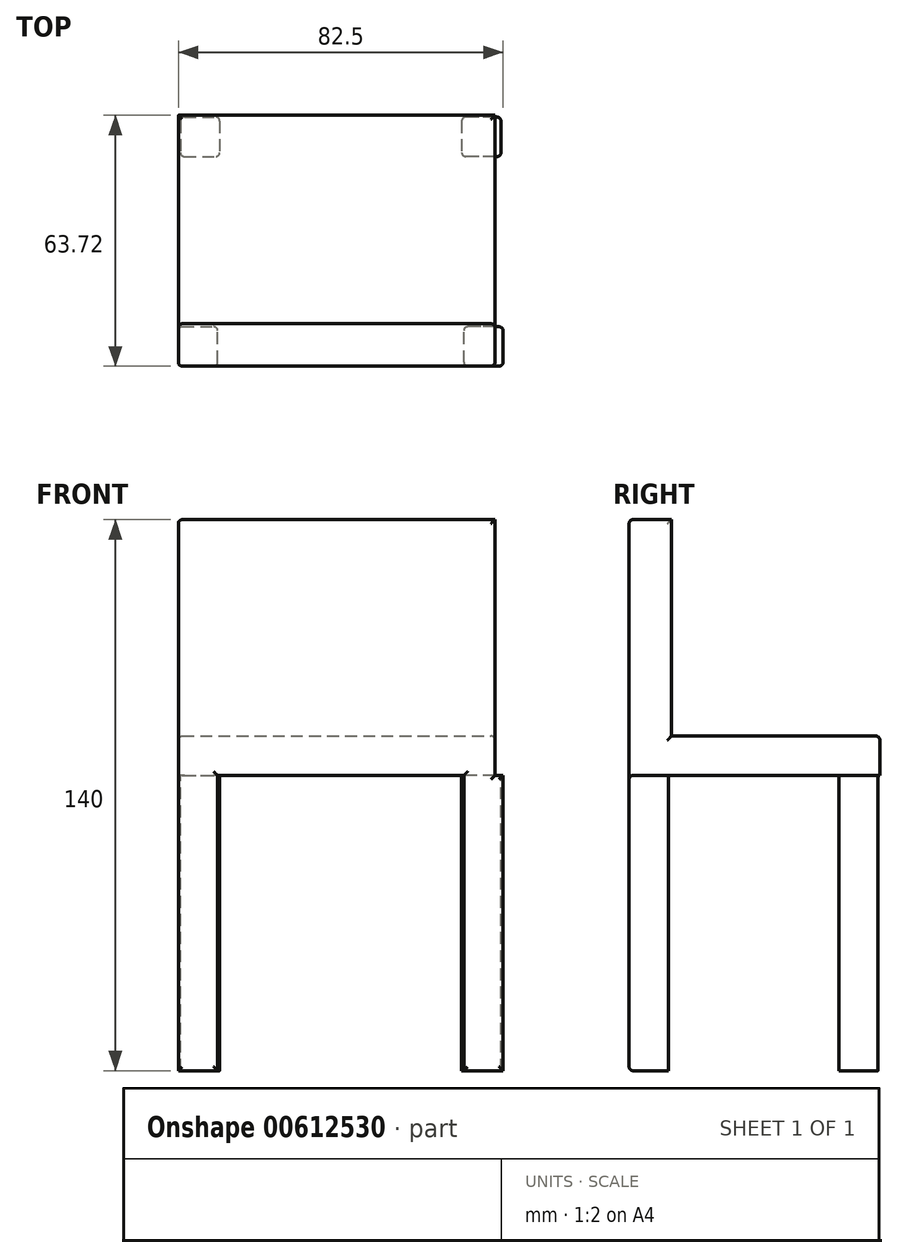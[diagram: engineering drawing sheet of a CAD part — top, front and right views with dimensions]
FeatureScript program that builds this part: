
annotation { "Feature Type Name" : "Feature", "Feature Type Description" : "" }
export const myFeature = defineFeature(function(context is Context, id is Id, definition is map)
    precondition{}
    {
        {
            var Q0;
            Q0=qCreatedBy(makeId("Top.planeOp"),FACE);
            var sketch = newSketch(context, id + "F0", { "sketchPlane" : qUnion([Q0])});
            skLineSegment(sketch, "E0.bottom", {"start": v(39.19, -35.62) * mm, "end": v(-41.25, -35.62) * mm});
            skLineSegment(sketch, "E0.top", {"start": v(39.19, 28.1) * mm, "end": v(-41.25, 28.1) * mm});
            skLineSegment(sketch, "E0.left", {"start": v(39.19, -35.62) * mm, "end": v(39.19, 28.1) * mm});
            skLineSegment(sketch, "E0.right", {"start": v(-41.25, -35.62) * mm, "end": v(-41.25, 28.1) * mm});
            skSolve(sketch);
        }
        {
            var Q0;
            Q0=makeQuery(id+"F0.imprint","IMPRINT",FACE,{"disambiguationData":[TD([[makeQuery(id+"F0.imprint","IMPRINT",EDGE,{"derivedFrom":sQuery(id+"F0.wireOp",EDGE,"E0.bottom")}),-1.0]])]});
            extrude(context, id + "F1", {"entities" : qUnion([Q0]), "depth" : 10 * mm, "offsetDistance" : 25 * mm});
        }
        {
            var Q0;
            Q0=qCreatedBy(makeId("Top.planeOp"),FACE);
            var sketch = newSketch(context, id + "F2", { "sketchPlane" : qUnion([Q0])});
            skLineSegment(sketch, "E1.bottom", {"start": v(-40.74, 27.64) * mm, "end": v(-30.74, 27.64) * mm});
            skLineSegment(sketch, "E1.top", {"start": v(-40.74, 17.64) * mm, "end": v(-30.74, 17.64) * mm});
            skLineSegment(sketch, "E1.left", {"start": v(-40.74, 27.64) * mm, "end": v(-40.74, 17.64) * mm});
            skLineSegment(sketch, "E1.right", {"start": v(-30.74, 27.64) * mm, "end": v(-30.74, 17.64) * mm});
            skSolve(sketch);
        }
        {
            var Q0;
            Q0=makeQuery(id+"F2.imprint","IMPRINT",FACE,{"disambiguationData":[TD([[makeQuery(id+"F2.imprint","IMPRINT",EDGE,{"derivedFrom":sQuery(id+"F2.wireOp",EDGE,"E1.bottom")}),-1.0]])]});
            extrude(context, id + "F3", {"entities" : qUnion([Q0]), "oppositeDirection" : true, "depth" : 75 * mm, "offsetDistance" : 25 * mm});
        }
        {
            var Q0;
            Q0=makeQuery(id+"F1.opExtrude","CAP_FACE",FACE,{"disambiguationData":[OSD([sQuery(id+"F0.wireOp",EDGE,"E0.bottom"),sQuery(id+"F0.wireOp",EDGE,"E0.top"),sQuery(id+"F0.wireOp",EDGE,"E0.left"),sQuery(id+"F0.wireOp",EDGE,"E0.right")])],"isStart":true});
            var sketch = newSketch(context, id + "F4", { "sketchPlane" : qUnion([Q0])});
            skLineSegment(sketch, "E2.bottom", {"start": v(-41.25, 35.62) * mm, "end": v(-31.25, 35.62) * mm});
            skLineSegment(sketch, "E2.top", {"start": v(-41.25, 25.62) * mm, "end": v(-31.25, 25.62) * mm});
            skLineSegment(sketch, "E2.left", {"start": v(-41.25, 35.62) * mm, "end": v(-41.25, 25.62) * mm});
            skLineSegment(sketch, "E2.right", {"start": v(-31.25, 35.62) * mm, "end": v(-31.25, 25.62) * mm});
            skSolve(sketch);
        }
        {
            var Q0;
            Q0=makeQuery(id+"F4.imprint","IMPRINT",FACE,{"disambiguationData":[TD([[makeQuery(id+"F4.imprint","IMPRINT",EDGE,{"derivedFrom":sQuery(id+"F4.wireOp",EDGE,"E2.bottom")}),1.0]])]});
            extrude(context, id + "F5", {"entities" : qUnion([Q0]), "depth" : 75 * mm, "offsetDistance" : 25 * mm});
        }
        {
            var Q0;
            Q0=makeQuery(id+"F3.opExtrude","SWEPT_BODY",BODY,{"disambiguationData":[OSD([sQuery(id+"F2.wireOp",EDGE,"E1.bottom"),sQuery(id+"F2.wireOp",EDGE,"E1.top"),sQuery(id+"F2.wireOp",EDGE,"E1.left"),sQuery(id+"F2.wireOp",EDGE,"E1.right")])]});
            var Q1;
            Q1=makeQuery(id+"F5.opExtrude","SWEPT_BODY",BODY,{"disambiguationData":[OSD([sQuery(id+"F4.wireOp",EDGE,"E2.bottom"),sQuery(id+"F4.wireOp",EDGE,"E2.top"),sQuery(id+"F4.wireOp",EDGE,"E2.left"),sQuery(id+"F4.wireOp",EDGE,"E2.right")])]});
            var Q2;
            Q2=qCreatedBy(makeId("Right.planeOp"),FACE);
            mirror(context, id + "F6", {"operationType" : NewBodyOperationType.ADD, "entities" : qUnion([Q0, Q1]), "mirrorPlane" : qUnion([Q2])});
        }
        {
            var Q0;
            Q0=makeQuery(id+"F1.opExtrude","CAP_FACE",FACE,{"disambiguationData":[OSD([sQuery(id+"F0.wireOp",EDGE,"E0.bottom"),sQuery(id+"F0.wireOp",EDGE,"E0.top"),sQuery(id+"F0.wireOp",EDGE,"E0.left"),sQuery(id+"F0.wireOp",EDGE,"E0.right")])],"isStart":false});
            var sketch = newSketch(context, id + "F7", { "sketchPlane" : qUnion([Q0])});
            skLineSegment(sketch, "E3.bottom", {"start": v(-41.25, -24.86) * mm, "end": v(39.19, -24.86) * mm});
            skLineSegment(sketch, "E3.top", {"start": v(-41.25, -35.62) * mm, "end": v(39.19, -35.62) * mm});
            skLineSegment(sketch, "E3.left", {"start": v(-41.25, -24.86) * mm, "end": v(-41.25, -35.62) * mm});
            skLineSegment(sketch, "E3.right", {"start": v(39.19, -24.86) * mm, "end": v(39.19, -35.62) * mm});
            skSolve(sketch);
        }
        {
            var Q0;
            Q0=makeQuery(id+"F7.imprint","IMPRINT",FACE,{"disambiguationData":[TD([[makeQuery(id+"F7.imprint","IMPRINT",EDGE,{"derivedFrom":sQuery(id+"F7.wireOp",EDGE,"E3.bottom")}),-1.0]])]});
            extrude(context, id + "F8", {"entities" : qUnion([Q0]), "operationType" : NewBodyOperationType.ADD, "depth" : 55 * mm, "offsetDistance" : 25 * mm});
        }
        {
            var Q0;
            Q0=makeQuery(id+"F8.boolean.opBoolean","MERGE",FACE,{"derivedFrom":[makeQuery(id+"F1.opExtrude","SWEPT_FACE",FACE,{"disambiguationData":[OSD([sQuery(id+"F0.wireOp",EDGE,"E0.left")])]}),makeQuery(id+"F8.opExtrude","SWEPT_FACE",FACE,{"disambiguationData":[OSD([sQuery(id+"F7.wireOp",EDGE,"E3.right")])]})]});
            var sketch = newSketch(context, id + "F9", { "sketchPlane" : qUnion([Q0])});
            skArc(sketch, "E4", {"start": v(0, 10) * mm, "mid": v(13.52, 54.32) * mm, "end": v(-24.86, 28.35) * mm});
            skSolve(sketch);
        }
        {
            var Q0;
            Q0=sQuery(id+"F9.wireOp",EDGE,"E4");
            extrude(context, id + "F10", {"bodyType" : ToolBodyType.SURFACE, "surfaceEntities" : qUnion([Q0]), "depth" : 5 * mm, "offsetDistance" : 25 * mm});
        }
        {
            var Q0;
            Q0=makeQuery(id+"F10.opExtrude","SWEPT_BODY",BODY,{"disambiguationData":[OSD([sQuery(id+"F9.wireOp",EDGE,"E4")])]});
            var Q1;
            Q1=qCreatedBy(makeId("Right.planeOp"),FACE);
            mirror(context, id + "F11", {"entities" : qUnion([Q0]), "mirrorPlane" : qUnion([Q1])});
        }
        {
            var Q0;
            Q0=makeQuery(id+"F3.opExtrude","SWEPT_EDGE",EDGE,{"disambiguationData":[OSD([sQuery(id+"F2.wireOp",EDGE,"E1.top"),sQuery(id+"F2.wireOp",EDGE,"E1.left")])]});
            var Q1;
            Q1=makeQuery(id+"F3.opExtrude","SWEPT_EDGE",EDGE,{"disambiguationData":[OSD([sQuery(id+"F2.wireOp",EDGE,"E1.bottom"),sQuery(id+"F2.wireOp",EDGE,"E1.left")])]});
            var Q2;
            Q2=makeQuery(id+"F5.opExtrude","SWEPT_EDGE",EDGE,{"disambiguationData":[OSD([sQuery(id+"F0.wireOp",EDGE,"E0.right"),sQuery(id+"F4.wireOp",EDGE,"E2.top"),sQuery(id+"F4.wireOp",EDGE,"E2.left")])]});
            var Q3;
            Q3=makeQuery(id+"F8.boolean.opBoolean","MERGE",EDGE,{"derivedFrom":[makeQuery(id+"F6.boolean.opBoolean","MERGE",EDGE,{"derivedFrom":[makeQuery(id+"F1.opExtrude","SWEPT_EDGE",EDGE,{"disambiguationData":[OSD([sQuery(id+"F0.wireOp",EDGE,"E0.bottom"),sQuery(id+"F0.wireOp",EDGE,"E0.right")])]}),makeQuery(id+"F5.opExtrude","SWEPT_EDGE",EDGE,{"disambiguationData":[OSD([sQuery(id+"F4.wireOp",EDGE,"E2.bottom"),sQuery(id+"F4.wireOp",EDGE,"E2.left")])]})]}),makeQuery(id+"F8.opExtrude","SWEPT_EDGE",EDGE,{"disambiguationData":[OSD([sQuery(id+"F7.wireOp",EDGE,"E3.top"),sQuery(id+"F7.wireOp",EDGE,"E3.left")])]})]});
            var Q4;
            Q4=makeQuery(id+"F8.opExtrude","CAP_EDGE",EDGE,{"disambiguationData":[OSD([sQuery(id+"F7.wireOp",EDGE,"E3.left")])],"isStart":false});
            var Q5;
            Q5=makeQuery(id+"F8.opExtrude","SWEPT_EDGE",EDGE,{"disambiguationData":[OSD([sQuery(id+"F0.wireOp",EDGE,"E0.right"),sQuery(id+"F7.wireOp",EDGE,"E3.bottom"),sQuery(id+"F7.wireOp",EDGE,"E3.left")])]});
            var Q6;
            Q6=makeQuery(id+"F1.opExtrude","CAP_EDGE",EDGE,{"disambiguationData":[OSD([sQuery(id+"F0.wireOp",EDGE,"E0.right")])],"isStart":false});
            var Q7;
            Q7=makeQuery(id+"F1.opExtrude","CAP_EDGE",EDGE,{"disambiguationData":[OSD([sQuery(id+"F0.wireOp",EDGE,"E0.top")])],"isStart":false});
            var Q8;
            Q8=makeQuery(id+"F6.opPattern","COPY",EDGE,{"derivedFrom":makeQuery(id+"F5.opExtrude","SWEPT_EDGE",EDGE,{"disambiguationData":[OSD([sQuery(id+"F4.wireOp",EDGE,"E2.top"),sQuery(id+"F4.wireOp",EDGE,"E2.right")])]}),"instanceName":"1"});
            var Q9;
            Q9=makeQuery(id+"F6.opPattern","COPY",EDGE,{"derivedFrom":makeQuery(id+"F5.opExtrude","SWEPT_EDGE",EDGE,{"disambiguationData":[OSD([sQuery(id+"F0.wireOp",EDGE,"E0.bottom"),sQuery(id+"F4.wireOp",EDGE,"E2.bottom"),sQuery(id+"F4.wireOp",EDGE,"E2.right")])]}),"instanceName":"1"});
            var Q10;
            Q10=makeQuery(id+"F6.opPattern","COPY",EDGE,{"derivedFrom":makeQuery(id+"F3.opExtrude","SWEPT_EDGE",EDGE,{"disambiguationData":[OSD([sQuery(id+"F2.wireOp",EDGE,"E1.bottom"),sQuery(id+"F2.wireOp",EDGE,"E1.right")])]}),"instanceName":"1"});
            var Q11;
            Q11=makeQuery(id+"F6.opPattern","COPY",EDGE,{"derivedFrom":makeQuery(id+"F3.opExtrude","SWEPT_EDGE",EDGE,{"disambiguationData":[OSD([sQuery(id+"F2.wireOp",EDGE,"E1.top"),sQuery(id+"F2.wireOp",EDGE,"E1.right")])]}),"instanceName":"1"});
            var Q12;
            Q12=makeQuery(id+"F1.opExtrude","CAP_EDGE",EDGE,{"disambiguationData":[OSD([sQuery(id+"F0.wireOp",EDGE,"E0.left")])],"isStart":false});
            var Q13;
            Q13=makeQuery(id+"F8.opExtrude","SWEPT_EDGE",EDGE,{"disambiguationData":[OSD([sQuery(id+"F0.wireOp",EDGE,"E0.left"),sQuery(id+"F7.wireOp",EDGE,"E3.bottom"),sQuery(id+"F7.wireOp",EDGE,"E3.right")])]});
            var Q14;
            Q14=makeQuery(id+"F8.boolean.opBoolean","MERGE",EDGE,{"derivedFrom":[makeQuery(id+"F1.opExtrude","SWEPT_EDGE",EDGE,{"disambiguationData":[OSD([sQuery(id+"F0.wireOp",EDGE,"E0.bottom"),sQuery(id+"F0.wireOp",EDGE,"E0.left")])]}),makeQuery(id+"F8.opExtrude","SWEPT_EDGE",EDGE,{"disambiguationData":[OSD([sQuery(id+"F7.wireOp",EDGE,"E3.top"),sQuery(id+"F7.wireOp",EDGE,"E3.right")])]})]});
            var Q15;
            Q15=makeQuery(id+"F5.opExtrude","SWEPT_EDGE",EDGE,{"disambiguationData":[OSD([sQuery(id+"F0.wireOp",EDGE,"E0.bottom"),sQuery(id+"F4.wireOp",EDGE,"E2.bottom"),sQuery(id+"F4.wireOp",EDGE,"E2.right")])]});
            var Q16;
            {var subQ0=makeQuery(id+"F5.opExtrude","SWEPT_FACE",FACE,{"disambiguationData":[OSD([sQuery(id+"F4.wireOp",EDGE,"E2.bottom")])]});Q16=makeQuery(id+"F8.boolean.opBoolean","MERGE",FACE,{"derivedFrom":[makeQuery(id+"F6.boolean.opBoolean","MERGE",FACE,{"derivedFrom":[makeQuery(id+"F1.opExtrude","SWEPT_FACE",FACE,{"disambiguationData":[OSD([sQuery(id+"F0.wireOp",EDGE,"E0.bottom")])]}),subQ0,makeQuery(id+"F6.opPattern","COPY",FACE,{"derivedFrom":subQ0,"instanceName":"1"})]}),makeQuery(id+"F8.opExtrude","SWEPT_FACE",FACE,{"disambiguationData":[OSD([sQuery(id+"F7.wireOp",EDGE,"E3.top")])]})]});}
            var Q17;
            Q17=makeQuery(id+"F3.opExtrude","SWEPT_EDGE",EDGE,{"disambiguationData":[OSD([sQuery(id+"F2.wireOp",EDGE,"E1.bottom"),sQuery(id+"F2.wireOp",EDGE,"E1.right")])]});
            var Q18;
            Q18=makeQuery(id+"F6.opPattern","COPY",EDGE,{"derivedFrom":makeQuery(id+"F3.opExtrude","SWEPT_EDGE",EDGE,{"disambiguationData":[OSD([sQuery(id+"F2.wireOp",EDGE,"E1.bottom"),sQuery(id+"F2.wireOp",EDGE,"E1.left")])]}),"instanceName":"1"});
            var Q19;
            Q19=makeQuery(id+"F6.opPattern","COPY",EDGE,{"derivedFrom":makeQuery(id+"F5.opExtrude","SWEPT_EDGE",EDGE,{"disambiguationData":[OSD([sQuery(id+"F0.wireOp",EDGE,"E0.right"),sQuery(id+"F4.wireOp",EDGE,"E2.top"),sQuery(id+"F4.wireOp",EDGE,"E2.left")])]}),"instanceName":"1"});
            var Q20;
            Q20=makeQuery(id+"F5.opExtrude","SWEPT_EDGE",EDGE,{"disambiguationData":[OSD([sQuery(id+"F4.wireOp",EDGE,"E2.top"),sQuery(id+"F4.wireOp",EDGE,"E2.right")])]});
            var Q21;
            Q21=makeQuery(id+"F3.opExtrude","SWEPT_EDGE",EDGE,{"disambiguationData":[OSD([sQuery(id+"F2.wireOp",EDGE,"E1.top"),sQuery(id+"F2.wireOp",EDGE,"E1.right")])]});
            var Q22;
            Q22=makeQuery(id+"F6.opPattern","COPY",EDGE,{"derivedFrom":makeQuery(id+"F3.opExtrude","SWEPT_EDGE",EDGE,{"disambiguationData":[OSD([sQuery(id+"F2.wireOp",EDGE,"E1.top"),sQuery(id+"F2.wireOp",EDGE,"E1.left")])]}),"instanceName":"1"});
            fillet(context, id + "F12", {"entities" : qUnion([Q0, Q1, Q2, Q3, Q4, Q5, Q6, Q7, Q8, Q9, Q10, Q11, Q12, Q13, Q14, Q15, Q16, Q17, Q18, Q19, Q20, Q21, Q22]), "radius" : 1 * mm, "tangentPropagation" : true, "allowEdgeOverflow" : false});
        }
    });
